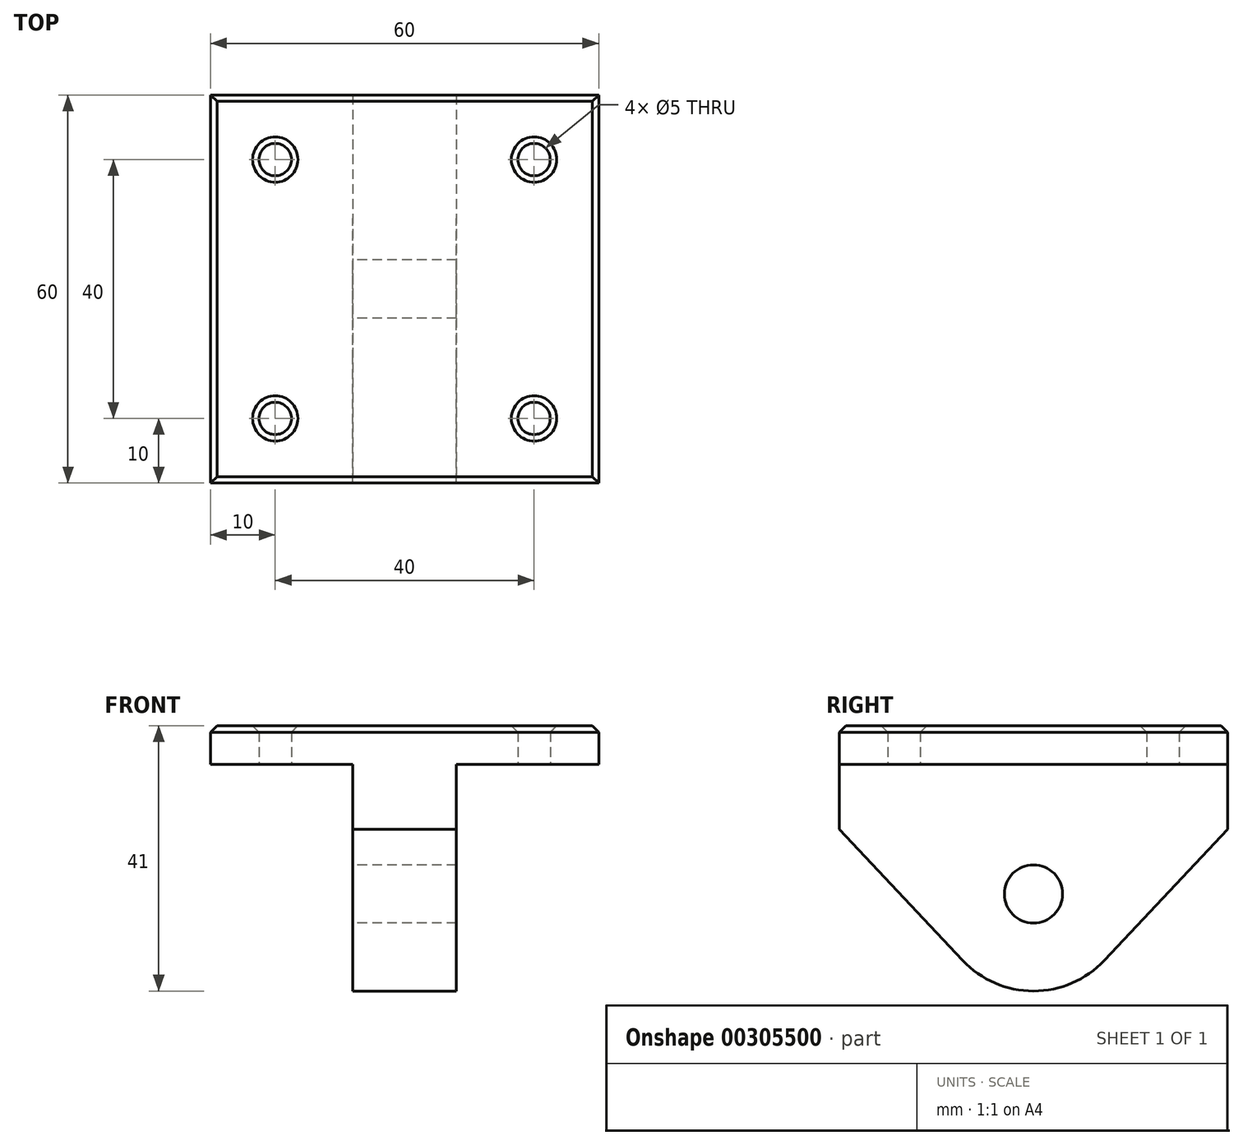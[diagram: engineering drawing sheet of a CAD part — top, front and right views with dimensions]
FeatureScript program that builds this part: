
annotation { "Feature Type Name" : "Feature", "Feature Type Description" : "" }
export const myFeature = defineFeature(function(context is Context, id is Id, definition is map)
    precondition{}
    {
        {
            var Q0;
            Q0=qCreatedBy(makeId("Right.planeOp"),FACE);
            var sketch = newSketch(context, id + "F0", { "sketchPlane" : qUnion([Q0])});
            skCircle(sketch, "E0", {"center": v(0, 0) * mm, "radius": 4.5 * mm});
            skArc(sketch, "E1", {"start": v(-10.93, -10.28) * mm, "mid": v(0, -15) * mm, "end": v(10.93, -10.28) * mm});
            skLineSegment(sketch, "E2", {"start": v(0, 0) * mm, "end": v(0, 20) * mm, "construction": true});
            skLineSegment(sketch, "E3", {"start": v(0, 20) * mm, "end": v(-30, 20) * mm});
            skLineSegment(sketch, "E4", {"start": v(-30, 20) * mm, "end": v(-30, 10) * mm});
            skLineSegment(sketch, "E5", {"start": v(-30, 10) * mm, "end": v(-10.93, -10.28) * mm});
            skLineSegment(sketch, "E6.MirrorCS", {"start": v(30, 10) * mm, "end": v(10.93, -10.28) * mm});
            skLineSegment(sketch, "E7.MirrorCS", {"start": v(30, 20) * mm, "end": v(30, 10) * mm});
            skLineSegment(sketch, "E8.MirrorCS", {"start": v(0, 20) * mm, "end": v(30, 20) * mm});
            skSolve(sketch);
        }
        {
            var Q0;
            Q0=makeQuery(id+"F0.imprint","IMPRINT",FACE,{"disambiguationData":[TD([[makeQuery(id+"F0.imprint","IMPRINT",EDGE,{"derivedFrom":sQuery(id+"F0.wireOp",EDGE,"E0")}),-1.0]])]});
            extrude(context, id + "F1", {"entities" : qUnion([Q0]), "endBound" : BoundingType.SYMMETRIC, "depth" : 16 * mm});
        }
        {
            var Q0;
            Q0=makeQuery(id+"F1.opExtrude","SWEPT_FACE",FACE,{"disambiguationData":[OSD([sQuery(id+"F0.wireOp",EDGE,"E3"),sQuery(id+"F0.wireOp",EDGE,"E8.MirrorCS")])]});
            var sketch = newSketch(context, id + "F2", { "sketchPlane" : qUnion([Q0])});
            skLineSegment(sketch, "E9", {"start": v(0, 30) * mm, "end": v(-30, 30) * mm});
            skLineSegment(sketch, "E10", {"start": v(-30, 30) * mm, "end": v(-30, -30) * mm});
            skLineSegment(sketch, "E11", {"start": v(-30, -30) * mm, "end": v(30, -30) * mm});
            skLineSegment(sketch, "E12", {"start": v(30, -30) * mm, "end": v(30, 30) * mm});
            skLineSegment(sketch, "E13", {"start": v(30, 30) * mm, "end": v(0, 30) * mm});
            skLineSegment(sketch, "E14", {"start": v(30, 30) * mm, "end": v(20, 30) * mm, "construction": true});
            skLineSegment(sketch, "E15", {"start": v(20, 30) * mm, "end": v(20, 20) * mm, "construction": true});
            skCircle(sketch, "E16", {"center": v(20, 20) * mm, "radius": 2.5 * mm});
            skCircle(sketch, "E17.MirrorC", {"center": v(-20, 20) * mm, "radius": 2.5 * mm});
            skCircle(sketch, "E18.MirrorC", {"center": v(-20, -20) * mm, "radius": 2.5 * mm});
            skCircle(sketch, "E19.MirrorC", {"center": v(20, -20) * mm, "radius": 2.5 * mm});
            skSolve(sketch);
        }
        {
            var Q0;
            {var subQ0=sQuery(id+"F0.wireOp",EDGE,"E8.MirrorCS");var subQ1=sQuery(id+"F0.wireOp",EDGE,"E3");var subQ2=makeQuery(id+"F1.opExtrude","CAP_EDGE",EDGE,{"disambiguationData":[OSD([subQ1,subQ0])],"isStart":true});Q0=makeQuery(id+"F2.imprint","IMPRINT",FACE,{"disambiguationData":[TD([[makeQuery(id+"F2.imprint","IMPRINT",EDGE,{"derivedFrom":subQ2}),1.0]])]});}
            var Q1;
            {var subQ2=sQuery(id+"F2.wireOp",EDGE,"E12");Q1=makeQuery(id+"F2.imprint","IMPRINT",FACE,{"disambiguationData":[TD([[makeQuery(id+"F2.imprint","IMPRINT",EDGE,{"derivedFrom":subQ2}),1.0]])]});}
            var Q2;
            {var subQ2=sQuery(id+"F2.wireOp",EDGE,"E10");Q2=makeQuery(id+"F2.imprint","IMPRINT",FACE,{"disambiguationData":[TD([[makeQuery(id+"F2.imprint","IMPRINT",EDGE,{"derivedFrom":subQ2}),1.0]])]});}
            extrude(context, id + "F3", {"entities" : qUnion([Q0, Q1, Q2]), "operationType" : NewBodyOperationType.ADD, "depth" : 6 * mm});
        }
        {
            var Q0;
            Q0=makeQuery(id+"F3.opExtrude","CAP_FACE",FACE,{"disambiguationData":[OSD([sQuery(id+"F2.wireOp",EDGE,"E9"),sQuery(id+"F2.wireOp",EDGE,"E10"),sQuery(id+"F2.wireOp",EDGE,"E11"),sQuery(id+"F2.wireOp",EDGE,"E12"),sQuery(id+"F2.wireOp",EDGE,"E13"),sQuery(id+"F2.wireOp",EDGE,"E16"),sQuery(id+"F2.wireOp",EDGE,"E17.MirrorC"),sQuery(id+"F2.wireOp",EDGE,"E18.MirrorC"),sQuery(id+"F2.wireOp",EDGE,"E19.MirrorC")])],"isStart":false});
            chamfer(context, id + "F4", {"entities" : qUnion([Q0]), "width" : 1 * mm, "tangentPropagation" : true});
        }
    });
